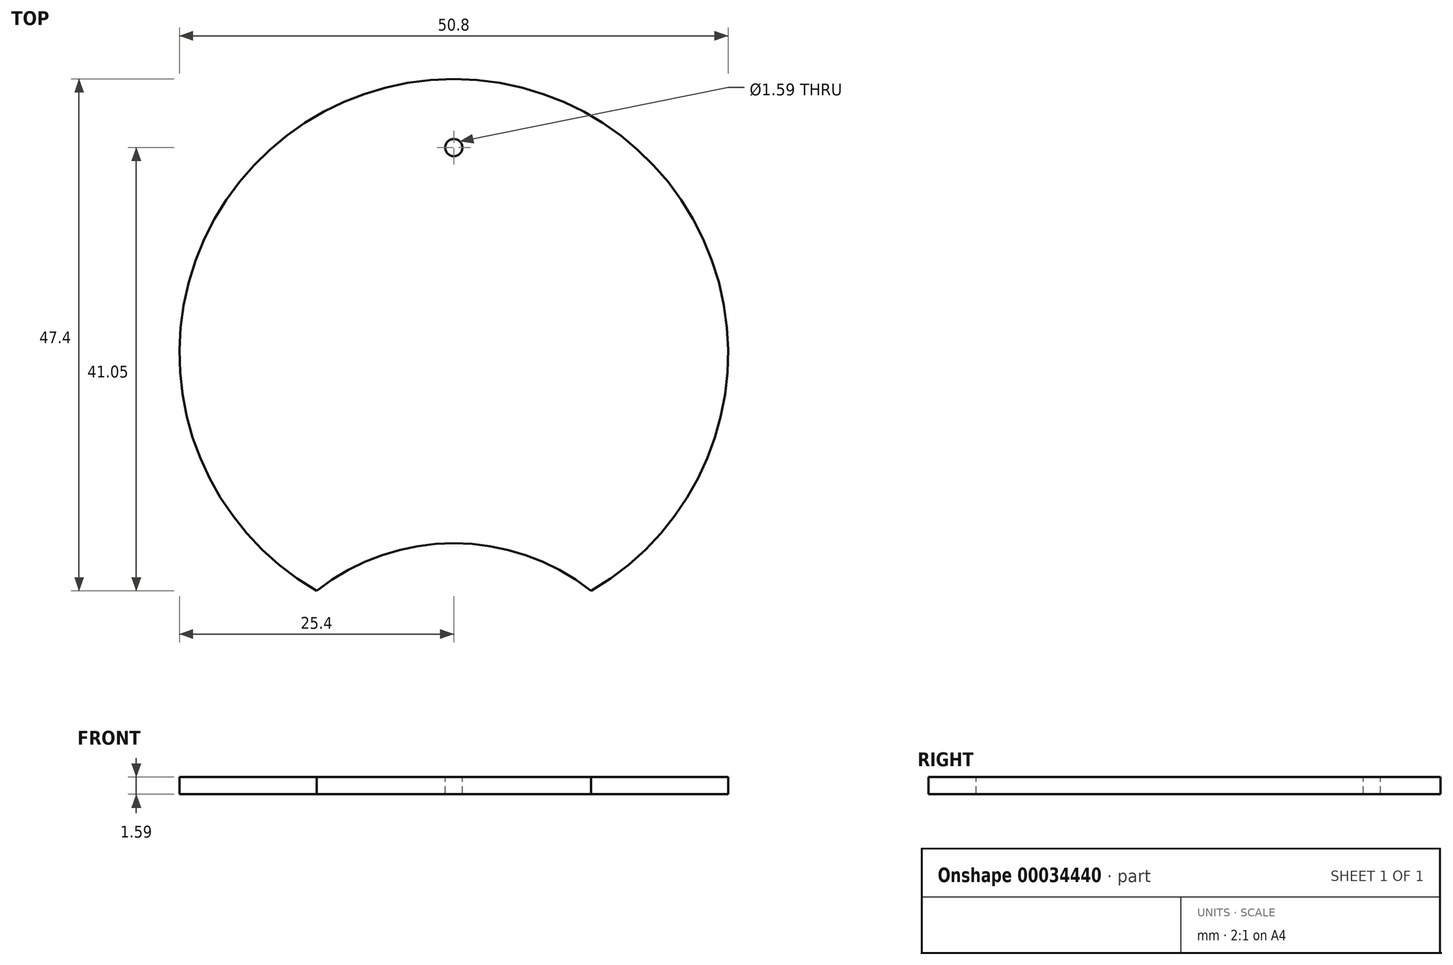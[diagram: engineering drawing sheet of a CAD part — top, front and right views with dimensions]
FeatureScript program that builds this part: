
annotation { "Feature Type Name" : "Feature", "Feature Type Description" : "" }
export const myFeature = defineFeature(function(context is Context, id is Id, definition is map)
    precondition{}
    {
        {
            var Q0;
            Q0=qCreatedBy(makeId("Top.planeOp"),FACE);
            var sketch = newSketch(context, id + "F0", { "sketchPlane" : qUnion([Q0])});
            skArc(sketch, "E0", {"start": v(-12.7, -22) * mm, "mid": v(0, -25.4) * mm, "end": v(12.7, -22) * mm, "construction": true});
            skArc(sketch, "E1", {"start": v(12.7, -22) * mm, "mid": v(0, 25.4) * mm, "end": v(-12.7, -22) * mm});
            skArc(sketch, "E2", {"start": v(12.7, -22) * mm, "mid": v(0, -17.6) * mm, "end": v(-12.7, -22) * mm});
            skArc(sketch, "E3", {"start": v(-12.7, -22) * mm, "mid": v(0, -58.6) * mm, "end": v(12.7, -22) * mm, "construction": true});
            skCircle(sketch, "E4", {"center": v(0, 19.05) * mm, "radius": 0.8 * mm});
            skSolve(sketch);
        }
        {
            var Q0;
            Q0=makeQuery(id+"F0.imprint","IMPRINT",FACE,{"disambiguationData":[TD([[makeQuery(id+"F0.imprint","IMPRINT",EDGE,{"derivedFrom":sQuery(id+"F0.wireOp",EDGE,"E1")}),1.0]])]});
            extrude(context, id + "F1", {"entities" : qUnion([Q0]), "oppositeDirection" : true, "depth" : 1.59 * mm, "offsetDistance" : 25.4 * mm});
        }
    });
